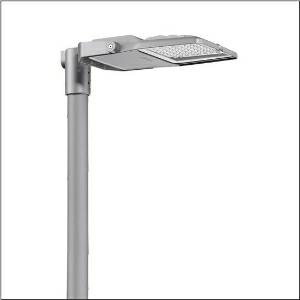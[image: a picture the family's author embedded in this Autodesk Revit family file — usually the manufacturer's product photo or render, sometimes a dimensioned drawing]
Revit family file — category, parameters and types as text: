
# Revit family: floodlight_fl_21_iq_mini___pl52_5xa7771c4d3a_e4a2
name_source: partatom
category: Lighting Fixtures
units: mm (PartAtom-declared; Revit-internal decimal feet)

## family parameters
Cut with Voids When Loaded = No
Host = Face
Light Source = No
Part Type = Normal
Room Calculation Point = No
Round Connector Dimension = Use Diameter
Shared = No

## types (1)
- --- (1 x LED, 12720 lm, 87.2 W, 4000K)
    Apparent Load = 87 VA
    CIE Flux Codes = 26 60 98 100 100
    Color Rendering = 70
    Color Temperature = 4000K
    Default Elevation = 1800 mm
    Description = Floodlight FL 21 iQ mini, floodlight, primary light control with lens, of PMMA, primary optical cover: protective disc, of toughened safety glass, transparent, light distribution: PL52, light emission: direct distribution, installation type: surface-mounted, LED, High Power LED, rated luminous flux: 12.720lm, luminous efficacy: 146lm/W, light colour: 740, colour temperature: 4000K, control gear: iQ Comfort/DALI, control: Auto-Match, Temp-Guard, Lumen-Switch, Night-Set, Smart-Wire, Light-Fading, Desk-Remote (wireless, voltage-free reading and setting of iQ features in the workshop via application-optimized NFC function/RFID function), optimised constant luminous flux control (CLO 2.0), with terminal, 6-pole, mains connection: 220..240V, AC, 50/60Hz, start of lifetime: 87W, end of service life: 92W, reduction: 40W, luminaire housing, of diecast aluminium, powder-coated, Siteco® metallic grey (DB 702S), corrosivity category C5 mid according to DIN EN ISO 12944, suitable for swimming pools, chlorine-resistant, sealing non-destructively replaceable, please order mast flange separately, mast bracket, of steel, galvanised, powder-coated, Siteco® metallic grey (DB 702S), protection rating (complete): IP66, insulation class (complete): insulation class II (safety insulation), certification: CE, ENEC, VDE, protection symbol: D, impact resistance: IK08, permissible operating ambient temperature: -40..+40°C, permissible operating ambient temperature for outdoor applications: -40..+50°C, standard: DIN EN 12944, LABS conformity tested according to VDMA 24364:2018-05, packaging unit: 1 piece

Light Distribution: PL52
    Height = 70 mm
    Lamp = 1 x LED
    Lamp Light Flux = 12720 lm
    Lamp Power = 87.2 W
    Lamp count = 1
    Length = 485 mm
    Luminous efficacy = 146 lm/W
    Manufacturer = Siteco
    ModVariant = No
    Model = 5XA7771C4D3A
    Number of Poles = 1
    OnlyDefault = Yes
    Power Factor = 1
    Product Name = Floodlight FL 21 iQ mini | PL52
    Product group = floodlight | pylon annexe
    ProductGroupID = 6200
    Protection Class = Protection class II
    Protection Degree = IP 66
    RLX_Detail_Level = 1
    RLX_Emergency_Light_Flux = 0 lm
    RLX_Emergency_Type = 0
    RLX_Emergency_Type_DB = No
    RlxData = <blob elided: 101533 chars, md5=f8252d5b>
    Socket = socket
    Standby Power = 0 W
    System Light Flux = 12720 lm
    System Power = 87 W
    Type Comments = factory setting: luminous flux: 100 % | dim-lin: 254 | 456 mA
    Type Image = l_1007125.jpg
    URL = http://relux.com
    VarID = @adj_164448
    Voltage = 0 V
    Weight = 0.00 kg
    Width = 337 mm

## geometry (parser evidence)
native form markers: Blend x4, Sweep x14
no freeform markers — native parametric forms only
